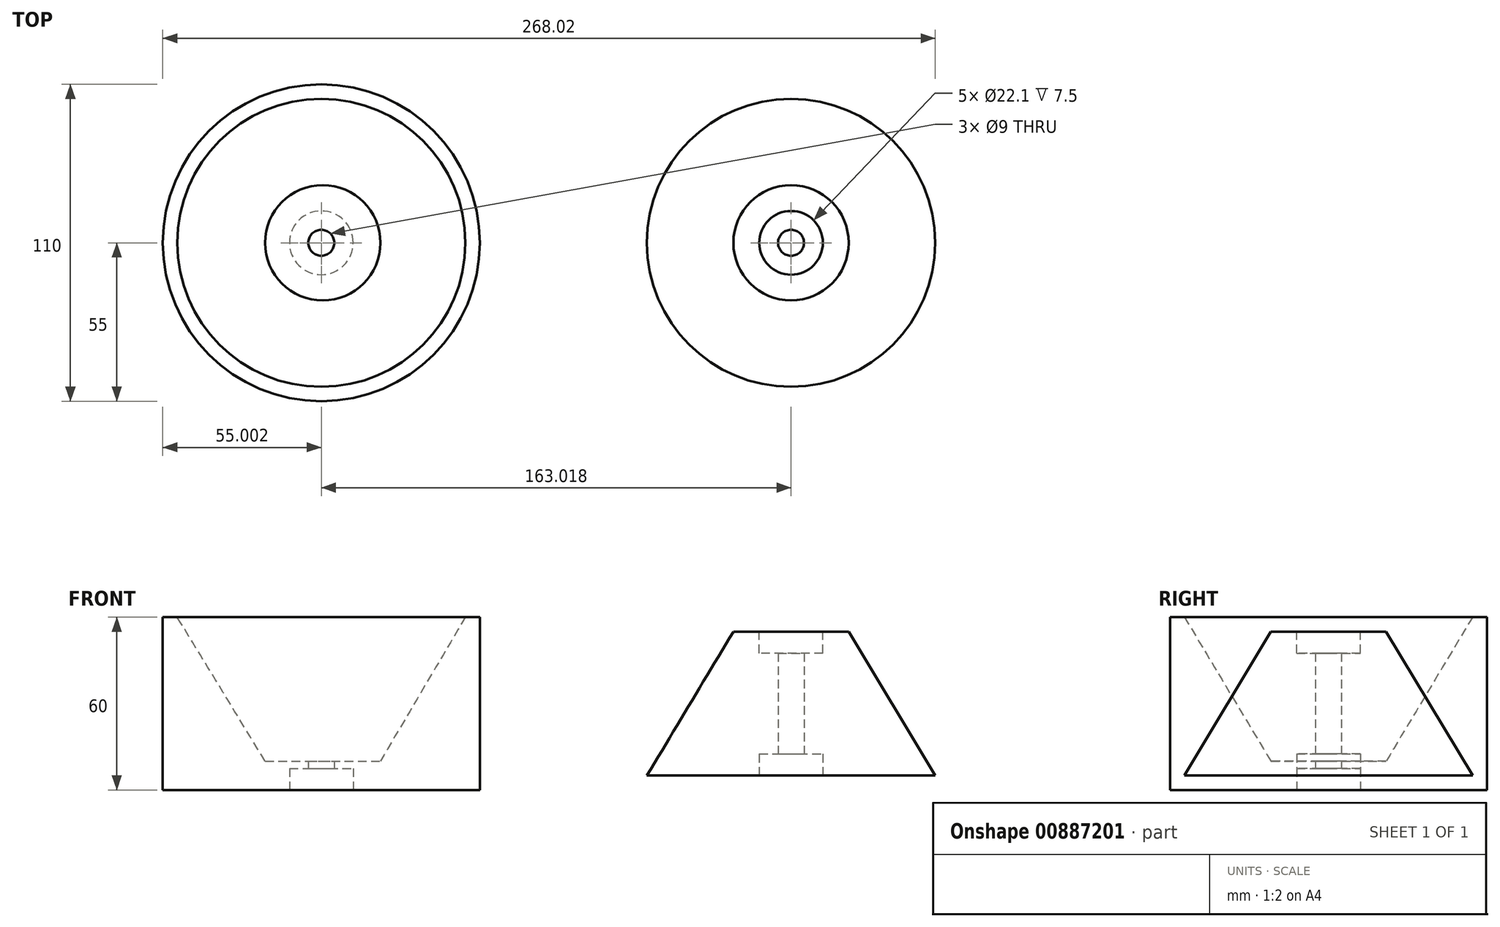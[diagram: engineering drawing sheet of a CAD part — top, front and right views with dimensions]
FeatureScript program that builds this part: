
annotation { "Feature Type Name" : "Feature", "Feature Type Description" : "" }
export const myFeature = defineFeature(function(context is Context, id is Id, definition is map)
    precondition{}
    {
        {
            var Q0;
            Q0=qCreatedBy(makeId("Right.planeOp"),FACE);
            var sketch = newSketch(context, id + "F0", { "sketchPlane" : qUnion([Q0])});
            skLineSegment(sketch, "E0", {"start": v(0, 0) * mm, "end": v(-50, 0) * mm});
            skLineSegment(sketch, "E1", {"start": v(0, 50) * mm, "end": v(-20, 50) * mm});
            skLineSegment(sketch, "E2", {"start": v(-20, 50) * mm, "end": v(-50, 0) * mm});
            skLineSegment(sketch, "E3", {"start": v(0, 0) * mm, "end": v(0, 50) * mm});
            skLineSegment(sketch, "E4", {"start": v(0, -48.77) * mm, "end": v(0, 74.03) * mm, "construction": true});
            skSolve(sketch);
        }
        {
            var Q0;
            Q0=makeQuery(id+"F0.imprint","IMPRINT",FACE,{"disambiguationData":[TD([[makeQuery(id+"F0.imprint","IMPRINT",EDGE,{"derivedFrom":sQuery(id+"F0.wireOp",EDGE,"E0")}),-1.0]])]});
            var Q1;
            Q1=sQuery(id+"F0.wireOp",EDGE,"E4");
            revolve(context, id + "F1", {"surfaceOperationType" : NewSurfaceOperationType.NEW, "entities" : qUnion([Q0]), "axis" : qUnion([Q1]), "revolveType" : RevolveType.FULL});
        }
        {
            var Q0;
            Q0=makeQuery(id+"F1.opRevolve","SWEPT_FACE",FACE,{"disambiguationData":[OSD([sQuery(id+"F0.wireOp",EDGE,"E0")])]});
            var sketch = newSketch(context, id + "F2", { "sketchPlane" : qUnion([Q0])});
            skCircle(sketch, "E5", {"center": v(0, 0) * mm, "radius": 11.05 * mm});
            skCircle(sketch, "E6", {"center": v(0, 0) * mm, "radius": 4.5 * mm});
            skSolve(sketch);
        }
        {
            var Q0;
            Q0=makeQuery(id+"F2.imprint","IMPRINT",FACE,{"disambiguationData":[TD([[makeQuery(id+"F2.imprint","IMPRINT",EDGE,{"derivedFrom":sQuery(id+"F2.wireOp",EDGE,"E6")}),1.0]])]});
            extrude(context, id + "F3", {"entities" : qUnion([Q0]), "operationType" : NewBodyOperationType.REMOVE, "endBound" : BoundingType.THROUGH_ALL, "oppositeDirection" : true, "depth" : 25 * mm, "offsetDistance" : 25 * mm});
        }
        {
            var Q0;
            Q0=makeQuery(id+"F2.imprint","IMPRINT",FACE,{"disambiguationData":[TD([[makeQuery(id+"F2.imprint","IMPRINT",EDGE,{"derivedFrom":sQuery(id+"F2.wireOp",EDGE,"E5")}),1.0]])]});
            var Q1;
            Q1=sQuery(id+"F2.wireOp",EDGE,"E5");
            extrude(context, id + "F4", {"entities" : qUnion([Q0]), "operationType" : NewBodyOperationType.REMOVE, "surfaceEntities" : qUnion([Q1]), "oppositeDirection" : true, "depth" : 7.5 * mm, "offsetDistance" : 25 * mm});
        }
        {
            var Q0;
            Q0=makeQuery(id+"F1.opRevolve","SWEPT_FACE",FACE,{"disambiguationData":[OSD([sQuery(id+"F0.wireOp",EDGE,"E1")])]});
            var sketch = newSketch(context, id + "F5", { "sketchPlane" : qUnion([Q0])});
            skCircle(sketch, "E7", {"center": v(0, 0) * mm, "radius": 11.05 * mm});
            skSolve(sketch);
        }
        {
            var Q0;
            Q0=makeQuery(id+"F5.imprint","IMPRINT",FACE,{"disambiguationData":[TD([[makeQuery(id+"F5.imprint","IMPRINT",EDGE,{"derivedFrom":sQuery(id+"F5.wireOp",EDGE,"E7")}),1.0]])]});
            extrude(context, id + "F6", {"entities" : qUnion([Q0]), "operationType" : NewBodyOperationType.REMOVE, "oppositeDirection" : true, "depth" : 7.5 * mm, "offsetDistance" : 25 * mm});
        }
        {
            var Q0;
            Q0=qCreatedBy(makeId("Top.planeOp"),FACE);
            var sketch = newSketch(context, id + "F7", { "sketchPlane" : qUnion([Q0])});
            skCircle(sketch, "E8", {"center": v(-163.02, 0) * mm, "radius": 55 * mm});
            skSolve(sketch);
        }
        {
            var Q0;
            Q0=makeQuery(id+"F7.imprint","IMPRINT",FACE,{"disambiguationData":[TD([[makeQuery(id+"F7.imprint","IMPRINT",EDGE,{"derivedFrom":sQuery(id+"F7.wireOp",EDGE,"E8")}),1.0]])]});
            extrude(context, id + "F8", {"entities" : qUnion([Q0]), "depth" : 55 * mm, "offsetDistance" : 25 * mm});
        }
        {
            var Q0;
            Q0=makeQuery(id+"F8.opExtrude","CAP_FACE",FACE,{"disambiguationData":[OSD([sQuery(id+"F7.wireOp",EDGE,"E8")])],"isStart":false});
            var sketch = newSketch(context, id + "F9", { "sketchPlane" : qUnion([Q0])});
            skCircle(sketch, "E9", {"center": v(-163.02, 0) * mm, "radius": 50 * mm});
            skSolve(sketch);
        }
        {
            var Q0;
            Q0=makeQuery(id+"F8.opExtrude","CAP_FACE",FACE,{"disambiguationData":[OSD([sQuery(id+"F7.wireOp",EDGE,"E8")])],"isStart":true});
            cPlane(context, id + "F10", {"entities" : qUnion([Q0]), "cplaneType" : CPlaneType.OFFSET, "offset" : 5 * mm, "oppositeDirection" : true, "width" : 150 * mm, "height" : 150 * mm});
        }
        {
            var Q0;
            Q0=qCreatedBy(id+"F10.planeOp",FACE);
            var sketch = newSketch(context, id + "F11", { "sketchPlane" : qUnion([Q0])});
            skCircle(sketch, "E10", {"center": v(-162.52, 0) * mm, "radius": 20 * mm});
            skSolve(sketch);
        }
        {
            var Q1;
            Q1 = qSketchRegion(id + "F11", true);
            var Q2;
            Q2=makeQuery(id+"F9.imprint","IMPRINT",FACE,{"disambiguationData":[TD([[makeQuery(id+"F9.imprint","IMPRINT",EDGE,{"derivedFrom":sQuery(id+"F9.wireOp",EDGE,"E9")}),1.0]])]});
            loft(context, id + "F12", {"operationType" : NewBodyOperationType.REMOVE, "sheetProfilesArray" : [{ "sheetProfileEntities" : qUnion([Q1]) }, { "sheetProfileEntities" : qUnion([Q2]) }]});
        }
        {
            var Q0;
            Q0=makeQuery(id+"F8.opExtrude","CAP_FACE",FACE,{"disambiguationData":[OSD([sQuery(id+"F7.wireOp",EDGE,"E8")])],"isStart":true});
            extrude(context, id + "F13", {"entities" : qUnion([Q0]), "operationType" : NewBodyOperationType.ADD, "depth" : 5 * mm, "offsetDistance" : 25 * mm});
        }
        {
            var Q0;
            Q0=makeQuery(id+"F13.opExtrude","CAP_FACE",FACE,{"disambiguationData":[OSD([sQuery(id+"F7.wireOp",EDGE,"E8")])],"isStart":false});
            var sketch = newSketch(context, id + "F14", { "sketchPlane" : qUnion([Q0])});
            skCircle(sketch, "E11", {"center": v(-163.02, 0) * mm, "radius": 11.05 * mm});
            skCircle(sketch, "E12", {"center": v(-163.02, 0) * mm, "radius": 4.5 * mm});
            skSolve(sketch);
        }
        {
            var Q0;
            Q0=makeQuery(id+"F14.imprint","IMPRINT",FACE,{"disambiguationData":[TD([[makeQuery(id+"F14.imprint","IMPRINT",EDGE,{"derivedFrom":sQuery(id+"F14.wireOp",EDGE,"E12")}),1.0]])]});
            extrude(context, id + "F15", {"entities" : qUnion([Q0]), "operationType" : NewBodyOperationType.REMOVE, "endBound" : BoundingType.THROUGH_ALL, "oppositeDirection" : true, "depth" : 25 * mm, "offsetDistance" : 25 * mm});
        }
        {
            var Q0;
            Q0=makeQuery(id+"F14.imprint","IMPRINT",FACE,{"disambiguationData":[TD([[makeQuery(id+"F14.imprint","IMPRINT",EDGE,{"derivedFrom":sQuery(id+"F14.wireOp",EDGE,"E11")}),1.0]])]});
            extrude(context, id + "F16", {"entities" : qUnion([Q0]), "operationType" : NewBodyOperationType.REMOVE, "oppositeDirection" : true, "depth" : 7.5 * mm, "offsetDistance" : 25 * mm});
        }
    });
